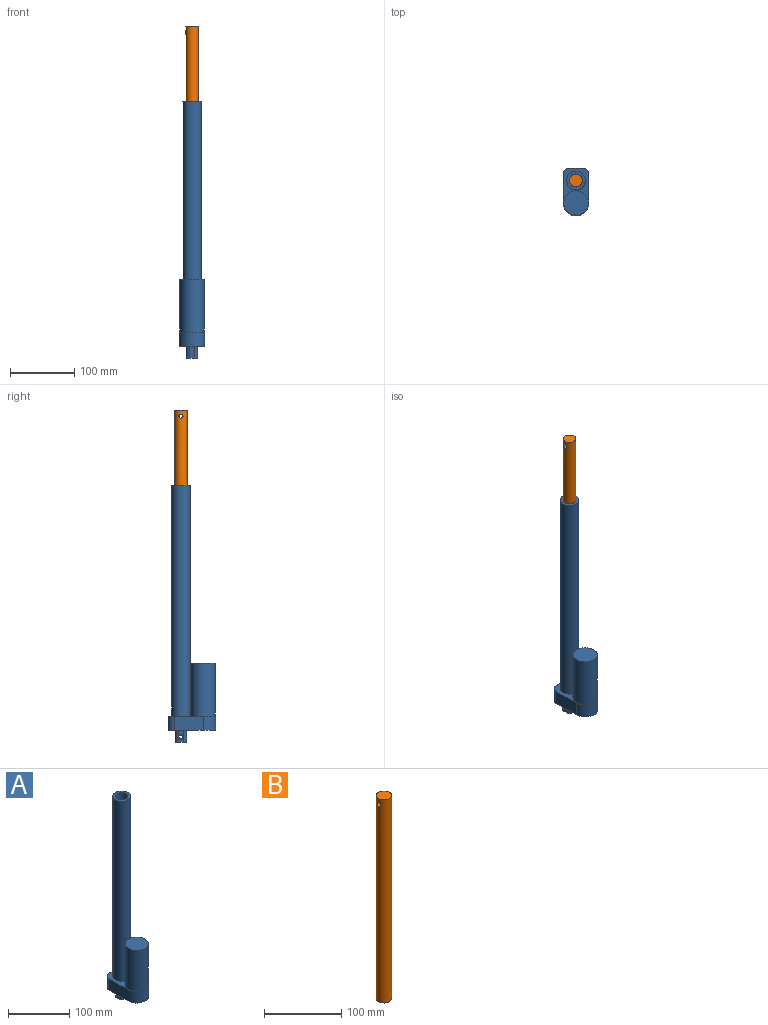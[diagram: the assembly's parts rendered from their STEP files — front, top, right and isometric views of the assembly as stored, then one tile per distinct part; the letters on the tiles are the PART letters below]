
ASSEMBLY  parts=2 mates=2
PART A: 24 faces, bbox 40x74.5x400.5 mm
  f0: plane 74.5x40mm, normal (0,0,-1), area 2480.6mm2, adj f5,f6,f7,f8,f9,f10,f12,f13
  f1: cylinder r=10mm len=360mm, axis (0,0,-1), area 22619.5mm2, adj f3,f11
  f2: cylinder r=14.7mm len=360mm, axis (0,0,-1), area 33250.6mm2, adj f3,f4
  f3: plane 29.4x29.4mm, normal (0,0,1), area 364.7mm2, adj f1,f2
  f4: plane 74.5x40mm, normal (0,0,1), area 952.4mm2, adj f2,f5,f6,f7,f8,f9,f10,f22
  f5: plane 22.5x20mm, normal (0,1,0), area 450mm2, adj f0,f4,f6,f10
  f6: cylinder r=10mm len=22.5mm, axis (0,0,1), area 353.4mm2, adj f0,f4,f5,f7
  f7: plane 44.5x22.5mm, normal (1,0,0), area 1001.2mm2, adj f0,f4,f6,f8
  f8: cylinder r=20mm len=40mm, axis (0,0,1), area 1413.7mm2, adj f0,f4,f7,f9
  f9: plane 44.5x22.5mm, normal (-1,0,0), area 1001.2mm2, adj f0,f4,f8,f10
  f10: cylinder r=10mm len=22.5mm, axis (0,0,1), area 353.4mm2, adj f0,f4,f5,f9
  f11: plane 20x20mm, normal (0,0,1), area 314.2mm2, adj f1
  f12: plane 18x7.5mm, normal (1,0,0), area 100.8mm2, adj f0,f13,f19,f20,f21
  f13: cylinder r=5mm len=18mm, axis (0,0,1), area 141.4mm2, adj f0,f12,f14,f20
  f14: plane 18x7.5mm, normal (0,-1,0), area 135mm2, adj f0,f13,f15,f20
  f15: cylinder r=5mm len=18mm, axis (0,0,1), area 141.4mm2, adj f0,f14,f16,f20
  f16: plane 18x7.5mm, normal (-1,0,0), area 100.8mm2, adj f0,f15,f17,f20,f21
  f17: cylinder r=5mm len=18mm, axis (0,0,1), area 141.4mm2, adj f0,f16,f18,f20
  f18: plane 18x7.5mm, normal (0,1,0), area 135mm2, adj f0,f17,f19,f20
  f19: cylinder r=5mm len=18mm, axis (0,0,1), area 141.4mm2, adj f0,f12,f18,f20
  f20: plane 17.5x17.5mm, normal (0,0,-1), area 284.8mm2, adj f12,f13,f14,f15,f16,f17,f18,f19
  f21: cylinder r=3.3mm len=17.5mm, axis (1,0,0), area 362.9mm2, adj f12,f16
  f22: cylinder r=19mm len=82mm, axis (0,0,-1), area 9789.2mm2, adj f4,f23
  f23: plane 38x38mm, normal (0,0,1), area 1134.1mm2, adj f22
PART B: 4 faces, bbox 20x20x322 mm
  f0: cylinder r=10mm len=322mm, axis (0,0,-1), area 20164.6mm2, adj f1,f2,f3
  f1: plane 20x20mm, normal (0,0,1), area 314.2mm2, adj f0
  f2: plane 20x20mm, normal (0,0,-1), area 314.2mm2, adj f0
  f3: cylinder r=3.25mm len=20mm, axis (-1,0,0), area 397.4mm2, adj f0
PLACE A t=(-224.3,-14.16,-12.61)mm fixed
PLACE B t=(-224.3,-14.16,142.65)mm
MATE cylindrical B.f0 <-> A.f1  axis (0,0,-1) through (-224.3,-14.16,142.65)mm
MATE parallel B.f3 <-> A.f21  axis (-1,0,0) through (-214.17,-14.16,455.1)mm
